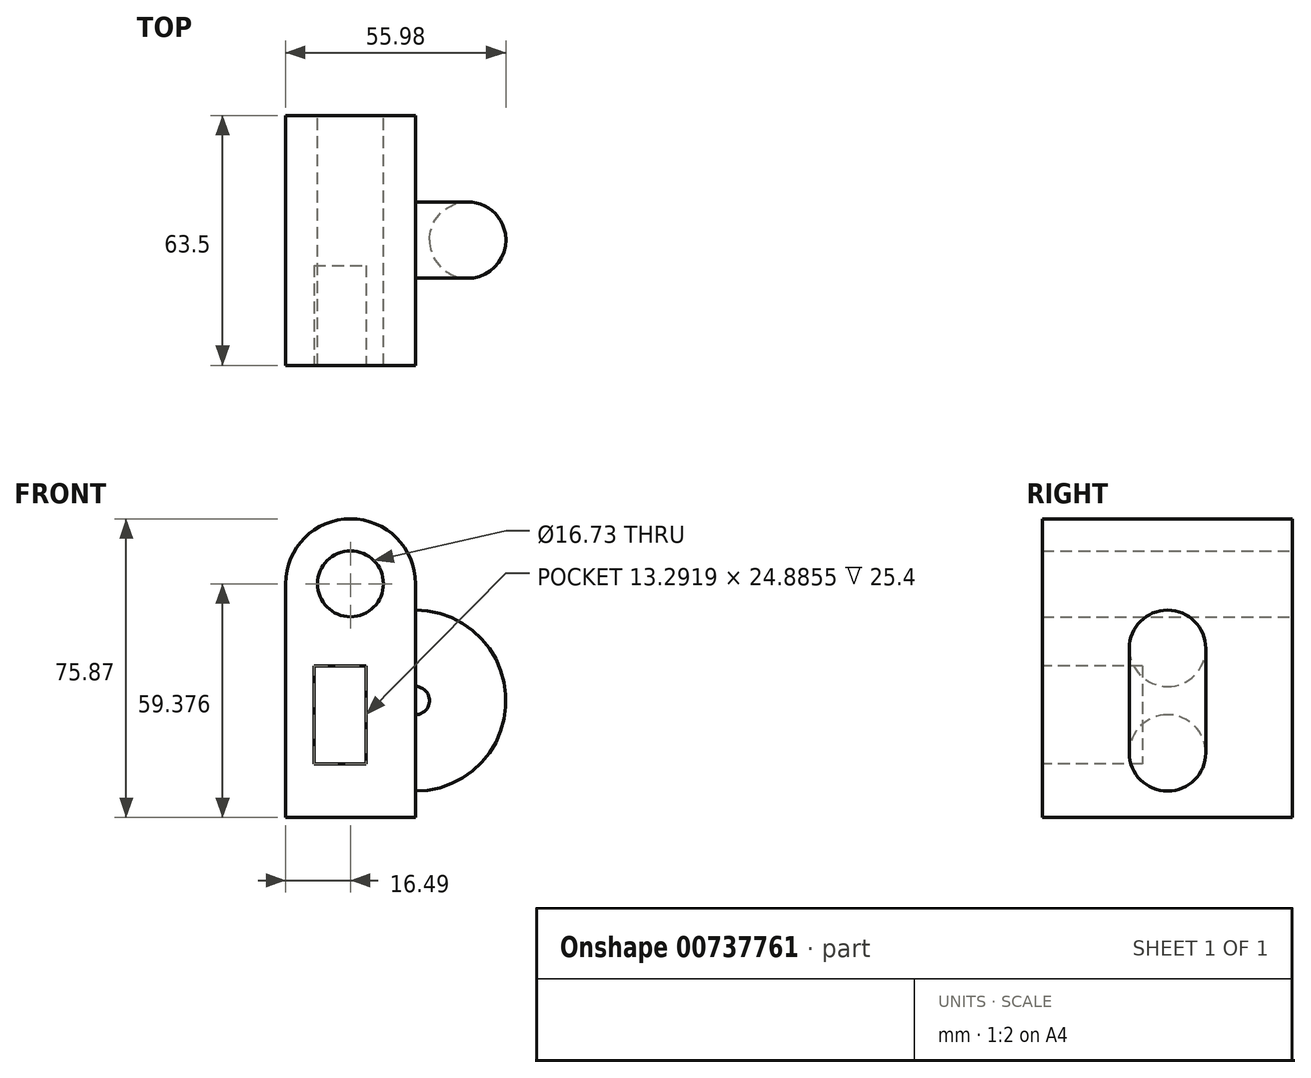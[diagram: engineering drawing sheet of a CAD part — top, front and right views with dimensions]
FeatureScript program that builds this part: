
annotation { "Feature Type Name" : "Feature", "Feature Type Description" : "" }
export const myFeature = defineFeature(function(context is Context, id is Id, definition is map)
    precondition{}
    {
        {
            var Q0;
            Q0=qCreatedBy(makeId("Front.planeOp"),FACE);
            var sketch = newSketch(context, id + "F0", { "sketchPlane" : qUnion([Q0])});
            skLineSegment(sketch, "E0.top", {"start": v(16.5, -29.69) * mm, "end": v(-16.5, -29.69) * mm});
            skLineSegment(sketch, "E0.left", {"start": v(16.5, 29.69) * mm, "end": v(16.5, -29.69) * mm});
            skLineSegment(sketch, "E0.right", {"start": v(-16.5, 29.69) * mm, "end": v(-16.5, -29.69) * mm});
            skPoint(sketch, "E0.middle", {"position": v(0, 0) * mm});
            skArc(sketch, "E1", {"start": v(16.5, 29.69) * mm, "mid": v(0, 46.18) * mm, "end": v(-16.5, 29.69) * mm});
            skCircle(sketch, "E2", {"center": v(0, 29.69) * mm, "radius": 8.36 * mm});
            skSolve(sketch);
        }
        {
            var Q0;
            Q0 = qSketchRegion(id + "F0", true);
            extrude(context, id + "F1", {"entities" : qUnion([Q0]), "depth" : 63.5 * mm, "offsetDistance" : 25.4 * mm});
        }
        {
            var Q0;
            Q0=makeQuery(id+"F1.opExtrude","CAP_FACE",FACE,{"disambiguationData":[OSD([sQuery(id+"F0.wireOp",EDGE,"E0.top"),sQuery(id+"F0.wireOp",EDGE,"E0.left"),sQuery(id+"F0.wireOp",EDGE,"E0.right"),sQuery(id+"F0.wireOp",EDGE,"E1"),sQuery(id+"F0.wireOp",EDGE,"E2")])],"isStart":false});
            var sketch = newSketch(context, id + "F2", { "sketchPlane" : qUnion([Q0])});
            skLineSegment(sketch, "E3.bottom", {"start": v(-9.3, 8.85) * mm, "end": v(4, 8.85) * mm});
            skLineSegment(sketch, "E3.top", {"start": v(-9.3, -16.04) * mm, "end": v(4, -16.04) * mm});
            skLineSegment(sketch, "E3.left", {"start": v(-9.3, 8.85) * mm, "end": v(-9.3, -16.04) * mm});
            skLineSegment(sketch, "E3.right", {"start": v(4, 8.85) * mm, "end": v(4, -16.04) * mm});
            skSolve(sketch);
        }
        {
            var Q0;
            Q0 = qSketchRegion(id + "F2", true);
            extrude(context, id + "F3", {"entities" : qUnion([Q0]), "operationType" : NewBodyOperationType.REMOVE, "oppositeDirection" : true, "depth" : 25.4 * mm, "offsetDistance" : 25.4 * mm});
        }
        {
            var Q0;
            Q0=makeQuery(id+"F1.opExtrude","SWEPT_FACE",FACE,{"disambiguationData":[OSD([sQuery(id+"F0.wireOp",EDGE,"E0.left")])]});
            var sketch = newSketch(context, id + "F4", { "sketchPlane" : qUnion([Q0])});
            skCircle(sketch, "E4", {"center": v(-31.67, 13.29) * mm, "radius": 9.7 * mm});
            skLineSegment(sketch, "E5", {"start": v(-63.5, 0) * mm, "end": v(0, 0) * mm});
            skSolve(sketch);
        }
        {
            var Q0;
            Q0=makeQuery(id+"F4.imprint","IMPRINT",FACE,{"disambiguationData":[TD([[makeQuery(id+"F4.imprint","IMPRINT",EDGE,{"derivedFrom":sQuery(id+"F4.wireOp",EDGE,"E4")}),1.0]])]});
            var Q1;
            Q1 = qSketchRegion(id + "Fb0mNYyrLIXzYpU_1", true);
            var Q2;
            Q2=sQuery(id+"F4.wireOp",EDGE,"E5");
            revolve(context, id + "F5", {"operationType" : NewBodyOperationType.ADD, "surfaceOperationType" : NewSurfaceOperationType.NEW, "entities" : qUnion([Q0, Q1]), "axis" : qUnion([Q2]), "revolveType" : RevolveType.ONE_DIRECTION, "angle" : 180 * degree});
        }
    });
